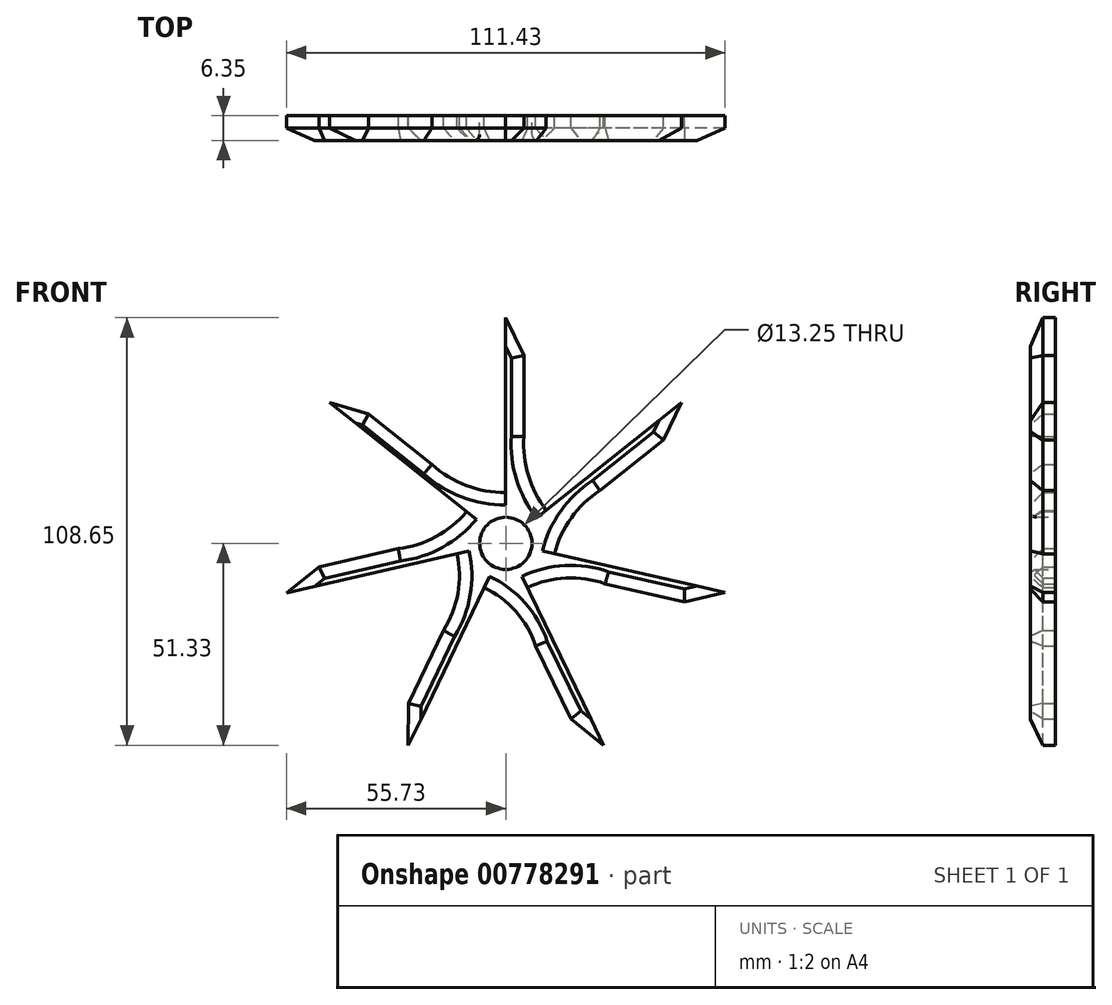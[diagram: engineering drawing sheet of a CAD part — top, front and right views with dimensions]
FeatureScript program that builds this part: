
annotation { "Feature Type Name" : "Feature", "Feature Type Description" : "" }
export const myFeature = defineFeature(function(context is Context, id is Id, definition is map)
    precondition{}
    {
        {
            var Q0;
            Q0=qCreatedBy(makeId("Front.planeOp"),FACE);
            var sketch = newSketch(context, id + "F0", { "sketchPlane" : qUnion([Q0])});
            skLineSegment(sketch, "E0", {"start": v(-0.02, 0.17) * mm, "end": v(-0.02, 65.94) * mm, "construction": true});
            skLineSegment(sketch, "E1", {"start": v(-0.02, 0.17) * mm, "end": v(62.98, 50.43) * mm, "construction": true});
            skLineSegment(sketch, "E2", {"start": v(-0.02, 0.17) * mm, "end": v(85.47, -19.31) * mm, "construction": true});
            skLineSegment(sketch, "E3", {"start": v(-0.02, 0.17) * mm, "end": v(34.2, -70.81) * mm, "construction": true});
            skLineSegment(sketch, "E4", {"start": v(-0.02, 0.17) * mm, "end": v(-35.22, -73.03) * mm, "construction": true});
            skLineSegment(sketch, "E5", {"start": v(-0.02, 0.17) * mm, "end": v(-77.45, -17.56) * mm, "construction": true});
            skLineSegment(sketch, "E6", {"start": v(-0.02, 0.17) * mm, "end": v(-64.01, 51.1) * mm, "construction": true});
            skCircle(sketch, "E7", {"center": v(-0.02, 0.17) * mm, "radius": 38.1 * mm, "construction": true});
            skCircle(sketch, "E8", {"center": v(-0.02, 0.17) * mm, "radius": 57.15 * mm, "construction": true});
            skCircle(sketch, "E9", {"center": v(-0.02, 38.27) * mm, "radius": 25.4 * mm, "construction": true});
            skCircle(sketch, "E10", {"center": v(29.76, 23.93) * mm, "radius": 25.4 * mm, "construction": true});
            skCircle(sketch, "E11", {"center": v(37.13, -8.3) * mm, "radius": 25.4 * mm, "construction": true});
            skCircle(sketch, "E12", {"center": v(16.52, -34.15) * mm, "radius": 25.4 * mm, "construction": true});
            skCircle(sketch, "E13", {"center": v(-16.53, -34.17) * mm, "radius": 25.4 * mm, "construction": true});
            skCircle(sketch, "E14", {"center": v(-37.16, -8.33) * mm, "radius": 25.4 * mm, "construction": true});
            skCircle(sketch, "E15", {"center": v(-29.83, 23.9) * mm, "radius": 25.4 * mm, "construction": true});
            skCircle(sketch, "E16", {"center": v(-0.02, 0.17) * mm, "radius": 9.53 * mm, "construction": true});
            skCircle(sketch, "E17", {"center": v(-0.02, 0.17) * mm, "radius": 27.33 * mm, "construction": true});
            skCircle(sketch, "E18", {"center": v(-0.02, 0.17) * mm, "radius": 47.78 * mm, "construction": true});
            skLineSegment(sketch, "E19", {"start": v(4.36, 55.4) * mm, "end": v(4.36, 8.63) * mm, "construction": true});
            skLineSegment(sketch, "E20", {"start": v(44.67, 30.22) * mm, "end": v(9.32, 2.02) * mm, "construction": true});
            skLineSegment(sketch, "E21", {"start": v(51.72, -16.12) * mm, "end": v(5.86, -5.67) * mm, "construction": true});
            skLineSegment(sketch, "E22", {"start": v(19.17, -49.73) * mm, "end": v(-0.3, -9.35) * mm, "construction": true});
            skLineSegment(sketch, "E23", {"start": v(-26.38, -44.54) * mm, "end": v(-7.64, -5.55) * mm, "construction": true});
            skLineSegment(sketch, "E24", {"start": v(-37.16, 34.7) * mm, "end": v(-4.4, 8.63) * mm, "construction": true});
            skLineSegment(sketch, "E25", {"start": v(-52.86, -7.43) * mm, "end": v(-9.24, 2.56) * mm, "construction": true});
            skLineSegment(sketch, "E26", {"start": v(-0.02, 57.32) * mm, "end": v(-0.02, 9.7) * mm});
            skArc(sketch, "E27", {"start": v(7.42, 6.11) * mm, "mid": v(4.24, 9.02) * mm, "end": v(-0.02, 9.7) * mm});
            skLineSegment(sketch, "E28", {"start": v(7.42, 6.11) * mm, "end": v(10.26, 8.37) * mm});
            skArc(sketch, "E29", {"start": v(4.56, 27.12) * mm, "mid": v(5.72, 17.23) * mm, "end": v(10.26, 8.37) * mm});
            skLineSegment(sketch, "E30", {"start": v(4.56, 27.12) * mm, "end": v(4.56, 47.73) * mm});
            skLineSegment(sketch, "E31", {"start": v(4.56, 47.73) * mm, "end": v(-0.02, 57.32) * mm});
            skLineSegment(sketch, "E32", {"start": v(44.65, 35.81) * mm, "end": v(7.42, 6.11) * mm});
            skArc(sketch, "E33", {"start": v(9.26, -1.95) * mm, "mid": v(9.25, 2.3) * mm, "end": v(7.42, 6.11) * mm});
            skLineSegment(sketch, "E34", {"start": v(9.26, -1.95) * mm, "end": v(12.36, -2.65) * mm});
            skArc(sketch, "E35", {"start": v(23.9, 13.4) * mm, "mid": v(16.63, 6.45) * mm, "end": v(12.36, -2.65) * mm});
            skLineSegment(sketch, "E36", {"start": v(23.9, 13.4) * mm, "end": v(40.02, 26.25) * mm});
            skLineSegment(sketch, "E37", {"start": v(40.02, 26.25) * mm, "end": v(44.65, 35.81) * mm});
            skLineSegment(sketch, "E38", {"start": v(55.7, -12.53) * mm, "end": v(9.26, -1.95) * mm});
            skArc(sketch, "E39", {"start": v(4.11, -8.4) * mm, "mid": v(7.49, -5.81) * mm, "end": v(9.26, -1.95) * mm});
            skLineSegment(sketch, "E40", {"start": v(4.11, -8.4) * mm, "end": v(5.5, -11.27) * mm});
            skArc(sketch, "E41", {"start": v(25.23, -10.29) * mm, "mid": v(15.26, -8.79) * mm, "end": v(5.5, -11.27) * mm});
            skLineSegment(sketch, "E42", {"start": v(25.23, -10.29) * mm, "end": v(45.33, -14.87) * mm});
            skLineSegment(sketch, "E43", {"start": v(45.33, -14.87) * mm, "end": v(55.7, -12.53) * mm});
            skLineSegment(sketch, "E44", {"start": v(24.8, -51.3) * mm, "end": v(4.11, -8.4) * mm});
            skArc(sketch, "E45", {"start": v(-4.15, -8.41) * mm, "mid": v(-0.02, -9.35) * mm, "end": v(4.11, -8.4) * mm});
            skLineSegment(sketch, "E46", {"start": v(-4.15, -8.41) * mm, "end": v(-5.53, -11.27) * mm});
            skArc(sketch, "E47", {"start": v(7.55, -26.1) * mm, "mid": v(2.57, -17.3) * mm, "end": v(-5.53, -11.27) * mm});
            skLineSegment(sketch, "E48", {"start": v(7.55, -26.1) * mm, "end": v(16.5, -44.66) * mm});
            skLineSegment(sketch, "E49", {"start": v(16.5, -44.66) * mm, "end": v(24.8, -51.3) * mm});
            skLineSegment(sketch, "E50", {"start": v(-24.79, -51.33) * mm, "end": v(-4.15, -8.41) * mm});
            skArc(sketch, "E51", {"start": v(-9.3, -1.95) * mm, "mid": v(-7.46, -5.77) * mm, "end": v(-4.15, -8.41) * mm});
            skLineSegment(sketch, "E52", {"start": v(-9.3, -1.95) * mm, "end": v(-12.4, -2.66) * mm});
            skArc(sketch, "E53", {"start": v(-15.83, -22.13) * mm, "mid": v(-12.19, -12.73) * mm, "end": v(-12.4, -2.66) * mm});
            skLineSegment(sketch, "E54", {"start": v(-15.83, -22.13) * mm, "end": v(-24.76, -40.7) * mm});
            skLineSegment(sketch, "E55", {"start": v(-24.76, -40.7) * mm, "end": v(-24.79, -51.33) * mm});
            skLineSegment(sketch, "E56", {"start": v(-55.73, -12.59) * mm, "end": v(-9.3, -1.95) * mm});
            skArc(sketch, "E57", {"start": v(-7.47, 6.1) * mm, "mid": v(-9.3, 2.28) * mm, "end": v(-9.3, -1.95) * mm});
            skLineSegment(sketch, "E58", {"start": v(-7.47, 6.1) * mm, "end": v(-9.96, 8.08) * mm});
            skArc(sketch, "E59", {"start": v(-27.31, -1.38) * mm, "mid": v(-17.73, 1.68) * mm, "end": v(-9.96, 8.08) * mm});
            skLineSegment(sketch, "E60", {"start": v(-27.31, -1.38) * mm, "end": v(-47.4, -5.98) * mm});
            skLineSegment(sketch, "E61", {"start": v(-47.4, -5.98) * mm, "end": v(-55.73, -12.59) * mm});
            skLineSegment(sketch, "E62", {"start": v(-44.74, 35.76) * mm, "end": v(-7.47, 6.1) * mm});
            skArc(sketch, "E63", {"start": v(-0.02, 9.7) * mm, "mid": v(-4.16, 8.75) * mm, "end": v(-7.47, 6.1) * mm});
            skLineSegment(sketch, "E64", {"start": v(-0.02, 9.7) * mm, "end": v(-0.02, 12.87) * mm});
            skArc(sketch, "E65", {"start": v(-18.77, 20.06) * mm, "mid": v(-10.07, 14.7) * mm, "end": v(-0.02, 12.87) * mm});
            skLineSegment(sketch, "E66", {"start": v(-18.77, 20.06) * mm, "end": v(-34.86, 32.87) * mm});
            skLineSegment(sketch, "E67", {"start": v(-34.86, 32.87) * mm, "end": v(-44.74, 35.76) * mm});
            skCircle(sketch, "E68", {"center": v(0, 0) * mm, "radius": 9.97 * mm});
            skCircle(sketch, "E69", {"center": v(0, 0) * mm, "radius": 6.63 * mm});
            skSolve(sketch);
        }
        {
            var Q0;
            {var subQ0=sQuery(id+"F0.wireOp",EDGE,"E65");Q0=makeQuery(id+"F0.imprint","IMPRINT",FACE,{"disambiguationData":[TD([[makeQuery(id+"F0.imprint","IMPRINT",EDGE,{"derivedFrom":subQ0}),-1.0]])]});}
            var Q1;
            {var subQ1=sQuery(id+"F0.wireOp",EDGE,"E26");Q1=makeQuery(id+"F0.imprint","IMPRINT",FACE,{"disambiguationData":[TD([[makeQuery(id+"F0.imprint","IMPRINT",EDGE,{"derivedFrom":subQ1}),1.0]])]});}
            var Q2;
            {var subQ0=sQuery(id+"F0.wireOp",EDGE,"E35");Q2=makeQuery(id+"F0.imprint","IMPRINT",FACE,{"disambiguationData":[TD([[makeQuery(id+"F0.imprint","IMPRINT",EDGE,{"derivedFrom":subQ0}),-1.0]])]});}
            var Q3;
            {var subQ0=sQuery(id+"F0.wireOp",EDGE,"E41");Q3=makeQuery(id+"F0.imprint","IMPRINT",FACE,{"disambiguationData":[TD([[makeQuery(id+"F0.imprint","IMPRINT",EDGE,{"derivedFrom":subQ0}),-1.0]])]});}
            var Q4;
            {var subQ0=sQuery(id+"F0.wireOp",EDGE,"E47");Q4=makeQuery(id+"F0.imprint","IMPRINT",FACE,{"disambiguationData":[TD([[makeQuery(id+"F0.imprint","IMPRINT",EDGE,{"derivedFrom":subQ0}),-1.0]])]});}
            var Q5;
            {var subQ0=sQuery(id+"F0.wireOp",EDGE,"E53");Q5=makeQuery(id+"F0.imprint","IMPRINT",FACE,{"disambiguationData":[TD([[makeQuery(id+"F0.imprint","IMPRINT",EDGE,{"derivedFrom":subQ0}),-1.0]])]});}
            var Q6;
            {var subQ0=sQuery(id+"F0.wireOp",EDGE,"E59");Q6=makeQuery(id+"F0.imprint","IMPRINT",FACE,{"disambiguationData":[TD([[makeQuery(id+"F0.imprint","IMPRINT",EDGE,{"derivedFrom":subQ0}),-1.0]])]});}
            var Q7;
            {var subQ0=sQuery(id+"F0.wireOp",EDGE,"E33");Q7=makeQuery(id+"F0.imprint","IMPRINT",FACE,{"disambiguationData":[TD([[makeQuery(id+"F0.imprint","IMPRINT",EDGE,{"derivedFrom":subQ0}),1.0]])]});}
            var Q8;
            {var subQ0=sQuery(id+"F0.wireOp",EDGE,"E33");Q8=makeQuery(id+"F0.imprint","IMPRINT",FACE,{"disambiguationData":[TD([[makeQuery(id+"F0.imprint","IMPRINT",EDGE,{"derivedFrom":subQ0}),-1.0]])]});}
            var Q9;
            {var subQ0=sQuery(id+"F0.wireOp",EDGE,"E39");Q9=makeQuery(id+"F0.imprint","IMPRINT",FACE,{"disambiguationData":[TD([[makeQuery(id+"F0.imprint","IMPRINT",EDGE,{"derivedFrom":subQ0}),-1.0]])]});}
            var Q10;
            {var subQ0=sQuery(id+"F0.wireOp",EDGE,"E45");Q10=makeQuery(id+"F0.imprint","IMPRINT",FACE,{"disambiguationData":[TD([[makeQuery(id+"F0.imprint","IMPRINT",EDGE,{"derivedFrom":subQ0}),-1.0]])]});}
            var Q11;
            {var subQ0=sQuery(id+"F0.wireOp",EDGE,"E51");Q11=makeQuery(id+"F0.imprint","IMPRINT",FACE,{"disambiguationData":[TD([[makeQuery(id+"F0.imprint","IMPRINT",EDGE,{"derivedFrom":subQ0}),-1.0]])]});}
            var Q12;
            {var subQ0=sQuery(id+"F0.wireOp",EDGE,"E57");Q12=makeQuery(id+"F0.imprint","IMPRINT",FACE,{"disambiguationData":[TD([[makeQuery(id+"F0.imprint","IMPRINT",EDGE,{"derivedFrom":subQ0}),-1.0]])]});}
            var Q13;
            {var subQ0=sQuery(id+"F0.wireOp",EDGE,"E63");Q13=makeQuery(id+"F0.imprint","IMPRINT",FACE,{"disambiguationData":[TD([[makeQuery(id+"F0.imprint","IMPRINT",EDGE,{"derivedFrom":subQ0}),-1.0]])]});}
            var Q14;
            {var subQ1=sQuery(id+"F0.wireOp",EDGE,"E27");var subQ3=sQuery(id+"F0.wireOp",EDGE,"E68");var subQ4=makeQuery(id+"F0.imprint","INTERSECT",VERTEX,{"derivedFrom":[subQ1,subQ3]});Q14=makeQuery(id+"F0.imprint","IMPRINT",FACE,{"disambiguationData":[TD([[makeQuery(id+"F0.imprint","IMPRINT",EDGE,{"disambiguationData":[TD([[subQ4,-1.0]])],"derivedFrom":subQ3}),1.0]])]});}
            var Q15;
            {var subQ1=sQuery(id+"F0.wireOp",EDGE,"E27");var subQ3=sQuery(id+"F0.wireOp",EDGE,"E68");var subQ4=makeQuery(id+"F0.imprint","INTERSECT",VERTEX,{"derivedFrom":[subQ1,subQ3]});Q15=makeQuery(id+"F0.imprint","IMPRINT",FACE,{"disambiguationData":[TD([[makeQuery(id+"F0.imprint","IMPRINT",EDGE,{"disambiguationData":[TD([[subQ4,1.0]])],"derivedFrom":subQ3}),1.0]])]});}
            extrude(context, id + "F1", {"entities" : qUnion([Q0, Q1, Q2, Q3, Q4, Q5, Q6, Q7, Q8, Q9, Q10, Q11, Q12, Q13, Q14, Q15]), "depth" : 6.35 * mm, "offsetDistance" : 25.4 * mm});
        }
        {
            var Q0;
            Q0=makeQuery(id+"F1.opExtrude","CAP_EDGE",EDGE,{"disambiguationData":[OSD([sQuery(id+"F0.wireOp",EDGE,"E66")])],"isStart":false});
            var Q1;
            Q1=makeQuery(id+"F1.opExtrude","CAP_EDGE",EDGE,{"disambiguationData":[OSD([sQuery(id+"F0.wireOp",EDGE,"E65")])],"isStart":false});
            var Q2;
            Q2=makeQuery(id+"F1.opExtrude","CAP_EDGE",EDGE,{"disambiguationData":[OSD([sQuery(id+"F0.wireOp",EDGE,"E30")])],"isStart":false});
            var Q3;
            Q3=makeQuery(id+"F1.opExtrude","CAP_EDGE",EDGE,{"disambiguationData":[OSD([sQuery(id+"F0.wireOp",EDGE,"E29")])],"isStart":false});
            var Q4;
            Q4=makeQuery(id+"F1.opExtrude","CAP_EDGE",EDGE,{"disambiguationData":[OSD([sQuery(id+"F0.wireOp",EDGE,"E35")])],"isStart":false});
            var Q5;
            Q5=makeQuery(id+"F1.opExtrude","CAP_EDGE",EDGE,{"disambiguationData":[OSD([sQuery(id+"F0.wireOp",EDGE,"E36")])],"isStart":false});
            var Q6;
            Q6=makeQuery(id+"F1.opExtrude","CAP_EDGE",EDGE,{"disambiguationData":[OSD([sQuery(id+"F0.wireOp",EDGE,"E41")])],"isStart":false});
            var Q7;
            Q7=makeQuery(id+"F1.opExtrude","CAP_EDGE",EDGE,{"disambiguationData":[OSD([sQuery(id+"F0.wireOp",EDGE,"E42")])],"isStart":false});
            var Q8;
            Q8=makeQuery(id+"F1.opExtrude","CAP_EDGE",EDGE,{"disambiguationData":[OSD([sQuery(id+"F0.wireOp",EDGE,"E47")])],"isStart":false});
            var Q9;
            Q9=makeQuery(id+"F1.opExtrude","CAP_EDGE",EDGE,{"disambiguationData":[OSD([sQuery(id+"F0.wireOp",EDGE,"E48")])],"isStart":false});
            var Q10;
            Q10=makeQuery(id+"F1.opExtrude","CAP_EDGE",EDGE,{"disambiguationData":[OSD([sQuery(id+"F0.wireOp",EDGE,"E54")])],"isStart":false});
            var Q11;
            Q11=makeQuery(id+"F1.opExtrude","CAP_EDGE",EDGE,{"disambiguationData":[OSD([sQuery(id+"F0.wireOp",EDGE,"E53")])],"isStart":false});
            var Q12;
            Q12=makeQuery(id+"F1.opExtrude","CAP_EDGE",EDGE,{"disambiguationData":[OSD([sQuery(id+"F0.wireOp",EDGE,"E60")])],"isStart":false});
            var Q13;
            Q13=makeQuery(id+"F1.opExtrude","CAP_EDGE",EDGE,{"disambiguationData":[OSD([sQuery(id+"F0.wireOp",EDGE,"E59")])],"isStart":false});
            chamfer(context, id + "F2", {"entities" : qUnion([Q0, Q1, Q2, Q3, Q4, Q5, Q6, Q7, Q8, Q9, Q10, Q11, Q12, Q13]), "width" : 3.17 * mm, "tangentPropagation" : true});
        }
        {
            var Q0;
            Q0=makeQuery(id+"F1.opExtrude","CAP_EDGE",EDGE,{"disambiguationData":[OSD([sQuery(id+"F0.wireOp",EDGE,"E49")])],"isStart":false});
            var Q1;
            Q1=makeQuery(id+"F1.opExtrude","CAP_EDGE",EDGE,{"disambiguationData":[OSD([sQuery(id+"F0.wireOp",EDGE,"E55")])],"isStart":false});
            var Q2;
            Q2=makeQuery(id+"F1.opExtrude","CAP_EDGE",EDGE,{"disambiguationData":[OSD([sQuery(id+"F0.wireOp",EDGE,"E61")])],"isStart":false});
            var Q3;
            Q3=makeQuery(id+"F1.opExtrude","CAP_EDGE",EDGE,{"disambiguationData":[OSD([sQuery(id+"F0.wireOp",EDGE,"E67")])],"isStart":false});
            var Q4;
            Q4=makeQuery(id+"F1.opExtrude","CAP_EDGE",EDGE,{"disambiguationData":[OSD([sQuery(id+"F0.wireOp",EDGE,"E31")])],"isStart":false});
            var Q5;
            Q5=makeQuery(id+"F1.opExtrude","CAP_EDGE",EDGE,{"disambiguationData":[OSD([sQuery(id+"F0.wireOp",EDGE,"E37")])],"isStart":false});
            var Q6;
            Q6=makeQuery(id+"F1.opExtrude","CAP_EDGE",EDGE,{"disambiguationData":[OSD([sQuery(id+"F0.wireOp",EDGE,"E43")])],"isStart":false});
            chamfer(context, id + "F3", {"entities" : qUnion([Q0, Q1, Q2, Q3, Q4, Q5, Q6]), "width" : 3.17 * mm, "tangentPropagation" : true});
        }
        {
            var Q0;
            Q0=makeQuery(id+"F1.opExtrude","CAP_EDGE",EDGE,{"disambiguationData":[OSD([sQuery(id+"F0.wireOp",EDGE,"E69")])],"isStart":false});
            fillet(context, id + "F4", {"entities" : qUnion([Q0]), "radius" : 1.59 * mm, "tangentPropagation" : true, "allowEdgeOverflow" : false});
        }
    });
